# Revit family: PRD_AR_WstBns_RODANHygieneWasteBin_RODX612
name_source: partatom
category: Specialty Equipment
revit_build: Autodesk Revit 2018 (Build: 20190510_1515(x64)
units: mm (PartAtom-declared; Revit-internal decimal feet)

## family parameters
Cut with Voids When Loaded = Yes
Host = Face
OmniClass Number = 23.40.20.31.11
OmniClass Title = Bins
Part Type = Normal
Room Calculation Point = No
Round Connector Dimension = Use Diameter
Shared = No

## types (1)
- RODX612
    AssetType = Fixed
    BIMObjectName = PRD_AR_WasteBins_RODANHygieneWasteBin_RODX612
    BagHolder = Integrated
    Category = Pr_40_50_07_96, Waste bins
    Default Elevation = 600 mm
    Description = Sanitary towel and disposal bin for wall mounting, stainless steel, surface satin finished, material thickness 0.8 mm, approx. 6 liter capacity, with integrated bag holder, self closing lid, with integrated storage for paper hygiene bags, can be combined with RODX191 hygiene bag dispenser for plastic bags, cylinder lock with KWC standard key, includes stainless steel screws and dowels.
    DispenserMaterial = PRD_AR_StainlessSteel_SatinFinished
    DurationUnit = year
    Features = stainless steel, surface satin finished
    FillingVolume = 6.00 liter
    Finish = satin finished
    GrossWeight = 5.46 kg
    IfcExportAs = IfcFurnitureType
    IfcExportType = USERDEFINED
    IntegralAccessories = incl. stainless steel screws and dowels
    IsBuiltIn = TRUE
    Lid = Yes
    Lock = Key-lock
    MainColor = stainless steel
    Manufacturer = KWC Group AG
    ManufacturerName = KWC Group AG
    ManufacturerURL = www.kwc.com
    Material = stainless steel
    MaterialCode = 1.4301
    MaterialThickness = 0.80 mm
    Model = RODX612
    ModelNumber = 2000101358
    ModelReference = RODX612
    NBSDescription = Waste bins
    NBSReference = 45-35-72/380
    Name = Hygiene Waste Bin RODX612
    NetWeight = 4.56 kg
    NominalDepth = 130 mm  [stored 0.426509 ft]
    NominalHeight = 469 mm
    NominalWidth = 350 mm  [stored 1.14829 ft]
    Offset = 0 mm  [stored 0 ft]
    ProductInformation = https://pim.kwc.com
    Size = 350 x 469 x 130 mm
    Style = Waste bin
    TypeOfFixing = Screw
    TypeOfMounting = Wall mounting
    URL = www.kwc.com
    Uniclass2015Code = Pr_40_50_07_96
    Uniclass2015Title = Waste bins
    Uniclass2015Version = Products v1.17
    Version = 1
    WarrantyDurationUnit = year

note: [stored X ft] marks values corroborated as IEEE doubles in the binary element streams (Revit-internal decimal feet)

## geometry (parser evidence)
native form markers: Sweep x6
no freeform markers — native parametric forms only
